# Revit family: PRD_AR_TltPprDspnsrs_STRATOSToiletSeatPaperDispenser_STRX680
name_source: partatom
category: Specialty Equipment
revit_build: Autodesk Revit 2018 (Build: 20190510_1515(x64)
units: mm (PartAtom-declared; Revit-internal decimal feet)

## family parameters
Cut with Voids When Loaded = No
Host = Face
OmniClass Number = 23.40.20.21.21
OmniClass Title = Toilet Paper Dispensers
Part Type = Normal
Room Calculation Point = No
Round Connector Dimension = Use Diameter
Shared = No

## types (1)
- STRX680
    AssetType = Fixed
    BIMObjectName = PRD_AR_ToiletPaperDispensers_STRATOSToiletSeatPaperDispenser_STRX680
    Category = Pr_40_70_22_90, Toilet paper dispensers
    Default Elevation = 700 mm  [stored 2.29659 ft]
    Description = Toilet seat paper dispenser for wall mounting, stainless steel, surface satin finished, front with InoxPlus surface refinement for the reduction of finger marks and better cleaning characteristics (easy to clean), material thickness 1.5 mm, curved front cover with oval aperture, cylinder lock with KWC standard key, for KWC seat paper or others, includes stainless steel screws and dowels.
    DispenserMaterial = PRD_AR_StainlessSteel_SatinFinished
    DurationUnit = year
    Features = stainless steel, surface satin finished
    FillingQuantity = 200
    FillingQuantityUom = Pieces
    Finish = satin finished
    GrossWeight = 3.36 kg
    IfcExportAs = IfcFurnitureType
    IfcExportType = USERDEFINED
    IntegralAccessories = incl. stainless steel screws and dowels
    IsBuiltIn = TRUE
    Lock = Key-lock
    MainColor = stainless steel
    Manufacturer = KWC Group AG
    ManufacturerName = KWC Group AG
    ManufacturerURL = www.kwc.com
    Material = stainless steel
    MaterialCode = 1.4301
    MaterialThickness = 1.50 mm
    Model = STRX680
    ModelNumber = 2000057401
    ModelReference = STRX680
    NBSDescription = Toilet paper bulk dispensers
    NBSReference = 45-35-72/366
    Name = Toilet seat paper dispenser STRX680
    NetWeight = 2.72 kg
    NominalDepth = 54 mm  [stored 0.177165 ft]
    NominalHeight = 263 mm  [stored 0.862861 ft]
    NominalWidth = 393 mm  [stored 1.28937 ft]
    ProductInformation = https://pim.kwc.com
    Size = 393 x 263 x 54 mm
    Style = dispenser
    SurfaceTreatment = InoxPlus (anti fingerprint)
    TypeOfConsumable = Toilet seat paper
    TypeOfFixing = Screw
    TypeOfMounting = Wall mounting
    TypeOfOperation = Manual operation
    URL = www.kwc.com
    Uniclass2015Code = Pr_40_70_22_90
    Uniclass2015Title = Toilet paper dispensers
    Uniclass2015Version = Products v1.10
    Version = 1
    WarrantyDurationUnit = year

note: [stored X ft] marks values corroborated as IEEE doubles in the binary element streams (Revit-internal decimal feet)

## geometry (parser evidence)
native form markers: Sweep x2
no freeform markers — native parametric forms only
